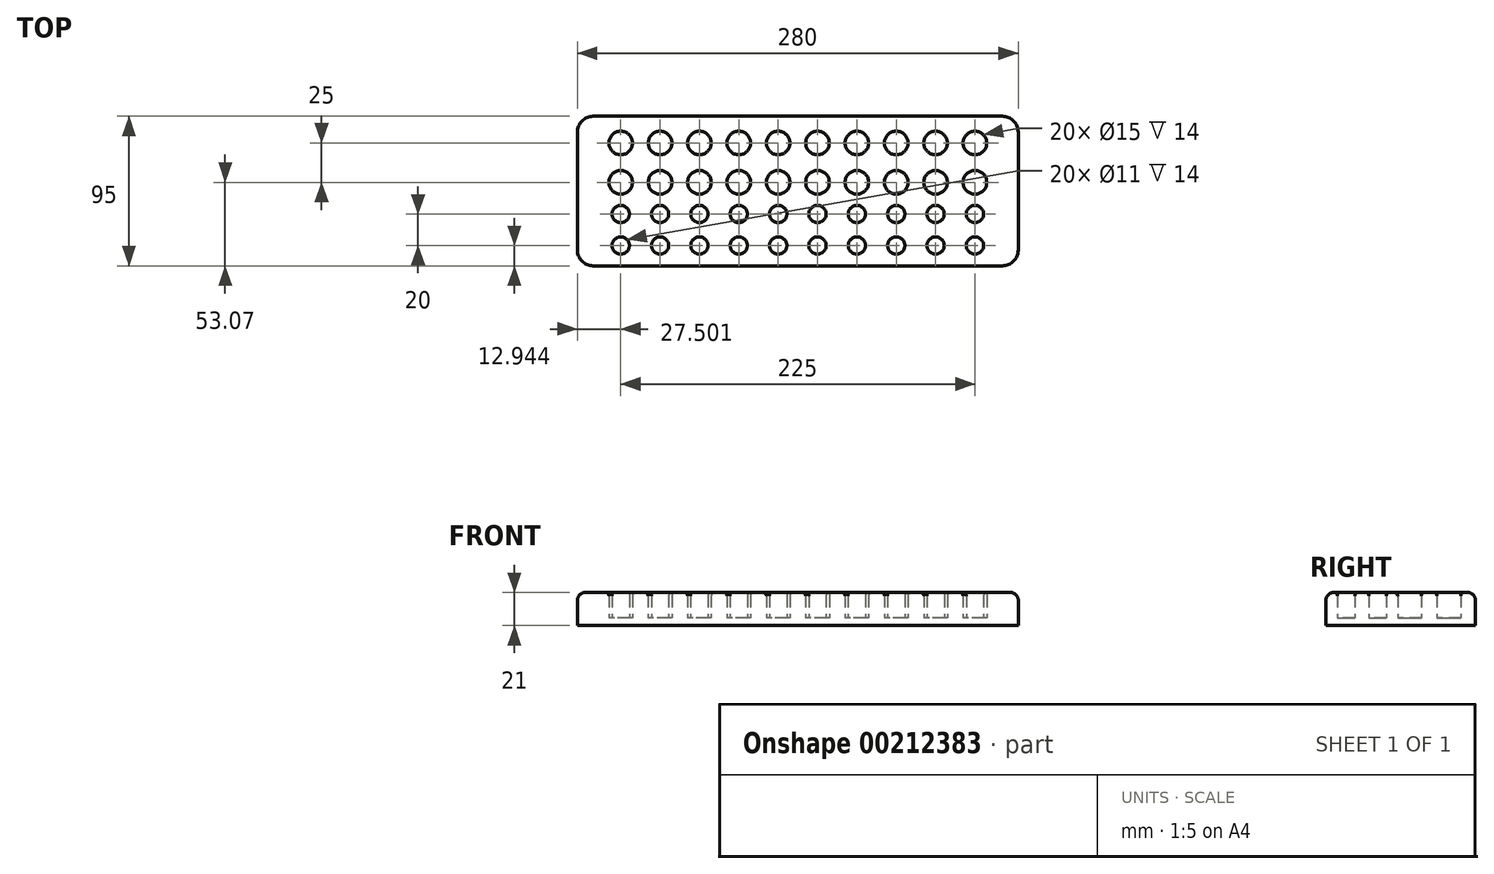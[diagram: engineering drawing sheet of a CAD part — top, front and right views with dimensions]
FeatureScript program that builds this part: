
annotation { "Feature Type Name" : "Feature", "Feature Type Description" : "" }
export const myFeature = defineFeature(function(context is Context, id is Id, definition is map)
    precondition{}
    {
        {
            var Q0;
            Q0=qCreatedBy(makeId("Top.planeOp"),FACE);
            var sketch = newSketch(context, id + "F0", { "sketchPlane" : qUnion([Q0])});
            skLineSegment(sketch, "E0.bottom", {"start": v(-133.18, 16.93) * mm, "end": v(126.82, 16.93) * mm});
            skLineSegment(sketch, "E0.top", {"start": v(-133.18, -78.07) * mm, "end": v(126.82, -78.07) * mm});
            skLineSegment(sketch, "E0.left", {"start": v(-143.18, 6.93) * mm, "end": v(-143.18, -68.07) * mm});
            skLineSegment(sketch, "E0.right", {"start": v(136.82, 6.93) * mm, "end": v(136.82, -68.07) * mm});
            skPoint(sketch, "E1.visualSharp", {"position": v(-143.18, 16.93) * mm});
            skArc(sketch, "E1.filletArc", {"start": v(-133.18, 16.93) * mm, "mid": v(-140.25, 14) * mm, "end": v(-143.18, 6.93) * mm});
            skPoint(sketch, "E2.visualSharp", {"position": v(136.82, 16.93) * mm});
            skArc(sketch, "E2.filletArc", {"start": v(136.82, 6.93) * mm, "mid": v(133.9, 14) * mm, "end": v(126.82, 16.93) * mm});
            skPoint(sketch, "E3.visualSharp", {"position": v(136.82, -78.07) * mm});
            skArc(sketch, "E3.filletArc", {"start": v(126.82, -78.07) * mm, "mid": v(133.9, -75.14) * mm, "end": v(136.82, -68.07) * mm});
            skPoint(sketch, "E4.visualSharp", {"position": v(-143.18, -78.07) * mm});
            skArc(sketch, "E4.filletArc", {"start": v(-143.18, -68.07) * mm, "mid": v(-140.25, -75.14) * mm, "end": v(-133.18, -78.07) * mm});
            skSolve(sketch);
        }
        {
            var Q0;
            Q0 = qSketchRegion(id + "F0", true);
            extrude(context, id + "F1", {"entities" : qUnion([Q0]), "depth" : 21 * mm});
        }
        {
            var Q0;
            Q0=qCreatedBy(makeId("Top.planeOp"),FACE);
            var sketch = newSketch(context, id + "F2", { "sketchPlane" : qUnion([Q0])});
            skCircle(sketch, "E5", {"center": v(-115.68, 0) * mm, "radius": 7.5 * mm});
            skCircle(sketch, "E6.0.1.0", {"center": v(-115.68, -25) * mm, "radius": 7.5 * mm});
            skCircle(sketch, "E6.1.0.0", {"center": v(-90.68, 0) * mm, "radius": 7.5 * mm});
            skCircle(sketch, "E6.1.1.0", {"center": v(-90.68, -25) * mm, "radius": 7.5 * mm});
            skCircle(sketch, "E6.2.0.0", {"center": v(-65.68, 0) * mm, "radius": 7.5 * mm});
            skCircle(sketch, "E6.2.1.0", {"center": v(-65.68, -25) * mm, "radius": 7.5 * mm});
            skCircle(sketch, "E6.3.0.0", {"center": v(-40.68, 0) * mm, "radius": 7.5 * mm});
            skCircle(sketch, "E6.3.1.0", {"center": v(-40.68, -25) * mm, "radius": 7.5 * mm});
            skCircle(sketch, "E6.4.0.0", {"center": v(-15.68, 0) * mm, "radius": 7.5 * mm});
            skCircle(sketch, "E6.4.1.0", {"center": v(-15.68, -25) * mm, "radius": 7.5 * mm});
            skCircle(sketch, "E6.5.0.0", {"center": v(9.32, 0) * mm, "radius": 7.5 * mm});
            skCircle(sketch, "E6.5.1.0", {"center": v(9.32, -25) * mm, "radius": 7.5 * mm});
            skCircle(sketch, "E6.6.0.0", {"center": v(34.32, 0) * mm, "radius": 7.5 * mm});
            skCircle(sketch, "E6.6.1.0", {"center": v(34.32, -25) * mm, "radius": 7.5 * mm});
            skCircle(sketch, "E6.7.0.0", {"center": v(59.32, 0) * mm, "radius": 7.5 * mm});
            skCircle(sketch, "E6.7.1.0", {"center": v(59.32, -25) * mm, "radius": 7.5 * mm});
            skCircle(sketch, "E6.8.0.0", {"center": v(84.32, 0) * mm, "radius": 7.5 * mm});
            skCircle(sketch, "E6.8.1.0", {"center": v(84.32, -25) * mm, "radius": 7.5 * mm});
            skCircle(sketch, "E6.9.0.0", {"center": v(109.32, 0) * mm, "radius": 7.5 * mm});
            skCircle(sketch, "E6.9.1.0", {"center": v(109.32, -25) * mm, "radius": 7.5 * mm});
            skLineSegment(sketch, "E6.direction1", {"start": v(-115.68, 0) * mm, "end": v(-90.68, 0) * mm, "construction": true});
            skLineSegment(sketch, "E6.direction2", {"start": v(-115.68, 0) * mm, "end": v(-115.68, -25) * mm, "construction": true});
            skLineSegment(sketch, "E7", {"start": v(109.32, 0) * mm, "end": v(136.82, 0) * mm, "construction": true});
            skLineSegment(sketch, "E8", {"start": v(-115.68, -12.5) * mm, "end": v(-143.18, -12.5) * mm, "construction": true});
            skCircle(sketch, "E9", {"center": v(-115.68, -45.13) * mm, "radius": 5.5 * mm});
            skLineSegment(sketch, "E10", {"start": v(-115.68, 0) * mm, "end": v(-115.68, -69.49) * mm, "construction": true});
            skCircle(sketch, "E11.0.1.0", {"center": v(-115.68, -65.13) * mm, "radius": 5.5 * mm});
            skCircle(sketch, "E11.1.0.0", {"center": v(-90.68, -45.13) * mm, "radius": 5.5 * mm});
            skCircle(sketch, "E11.1.1.0", {"center": v(-90.68, -65.13) * mm, "radius": 5.5 * mm});
            skCircle(sketch, "E11.2.0.0", {"center": v(-65.68, -45.13) * mm, "radius": 5.5 * mm});
            skCircle(sketch, "E11.2.1.0", {"center": v(-65.68, -65.13) * mm, "radius": 5.5 * mm});
            skCircle(sketch, "E11.3.0.0", {"center": v(-40.68, -45.13) * mm, "radius": 5.5 * mm});
            skCircle(sketch, "E11.3.1.0", {"center": v(-40.68, -65.13) * mm, "radius": 5.5 * mm});
            skCircle(sketch, "E11.4.0.0", {"center": v(-15.68, -45.13) * mm, "radius": 5.5 * mm});
            skCircle(sketch, "E11.4.1.0", {"center": v(-15.68, -65.13) * mm, "radius": 5.5 * mm});
            skCircle(sketch, "E11.5.0.0", {"center": v(9.32, -45.13) * mm, "radius": 5.5 * mm});
            skCircle(sketch, "E11.5.1.0", {"center": v(9.32, -65.13) * mm, "radius": 5.5 * mm});
            skCircle(sketch, "E11.6.0.0", {"center": v(34.32, -45.13) * mm, "radius": 5.5 * mm});
            skCircle(sketch, "E11.6.1.0", {"center": v(34.32, -65.13) * mm, "radius": 5.5 * mm});
            skCircle(sketch, "E11.7.0.0", {"center": v(59.32, -45.13) * mm, "radius": 5.5 * mm});
            skCircle(sketch, "E11.7.1.0", {"center": v(59.32, -65.13) * mm, "radius": 5.5 * mm});
            skCircle(sketch, "E11.8.0.0", {"center": v(84.32, -45.13) * mm, "radius": 5.5 * mm});
            skCircle(sketch, "E11.8.1.0", {"center": v(84.32, -65.13) * mm, "radius": 5.5 * mm});
            skCircle(sketch, "E11.9.0.0", {"center": v(109.32, -45.13) * mm, "radius": 5.5 * mm});
            skCircle(sketch, "E11.9.1.0", {"center": v(109.32, -65.13) * mm, "radius": 5.5 * mm});
            skLineSegment(sketch, "E11.direction1", {"start": v(-115.68, -45.13) * mm, "end": v(-90.68, -45.13) * mm, "construction": true});
            skLineSegment(sketch, "E11.direction2", {"start": v(-115.68, -45.13) * mm, "end": v(-115.68, -65.13) * mm, "construction": true});
            skSolve(sketch);
        }
        {
            var Q0;
            Q0 = qSketchRegion(id + "F2", true);
            var Q1;
            Q1=sQuery(id+"F2.wireOp",EDGE,"E6.3.0.0");
            var Q2;
            Q2=sQuery(id+"F2.wireOp",EDGE,"E6.8.0.0");
            var Q3;
            Q3=sQuery(id+"F2.wireOp",EDGE,"E11.3.1.0");
            var Q4;
            Q4=sQuery(id+"F2.wireOp",EDGE,"E6.2.1.0");
            var Q5;
            Q5=sQuery(id+"F2.wireOp",EDGE,"E6.2.0.0");
            var Q6;
            Q6=sQuery(id+"F2.wireOp",EDGE,"E11.4.0.0");
            var Q7;
            Q7=sQuery(id+"F2.wireOp",EDGE,"E11.2.0.0");
            var Q8;
            Q8=sQuery(id+"F2.wireOp",EDGE,"E6.1.1.0");
            var Q9;
            Q9=sQuery(id+"F2.wireOp",EDGE,"E6.1.0.0");
            var Q10;
            Q10=sQuery(id+"F2.wireOp",EDGE,"E11.5.1.0");
            var Q11;
            Q11=sQuery(id+"F2.wireOp",EDGE,"E6.0.1.0");
            var Q12;
            Q12=sQuery(id+"F2.wireOp",EDGE,"E5");
            var Q13;
            Q13=sQuery(id+"F2.wireOp",EDGE,"E11.7.0.0");
            var Q14;
            Q14=sQuery(id+"F2.wireOp",EDGE,"E6.7.1.0");
            var Q15;
            Q15=sQuery(id+"F2.wireOp",EDGE,"E6.7.0.0");
            var Q16;
            Q16=sQuery(id+"F2.wireOp",EDGE,"E11.1.0.0");
            var Q17;
            Q17=sQuery(id+"F2.wireOp",EDGE,"E11.9.0.0");
            var Q18;
            Q18=sQuery(id+"F2.wireOp",EDGE,"E6.6.1.0");
            var Q19;
            Q19=sQuery(id+"F2.wireOp",EDGE,"E11.9.1.0");
            var Q20;
            Q20=sQuery(id+"F2.wireOp",EDGE,"E11.1.1.0");
            var Q21;
            Q21=sQuery(id+"F2.wireOp",EDGE,"E11.7.1.0");
            var Q22;
            Q22=sQuery(id+"F2.wireOp",EDGE,"E6.8.1.0");
            var Q23;
            Q23=sQuery(id+"F2.wireOp",EDGE,"E9");
            var Q24;
            Q24=sQuery(id+"F2.wireOp",EDGE,"E11.6.0.0");
            var Q25;
            Q25=sQuery(id+"F2.wireOp",EDGE,"E11.2.1.0");
            var Q26;
            Q26=sQuery(id+"F2.wireOp",EDGE,"E6.3.1.0");
            var Q27;
            Q27=sQuery(id+"F2.wireOp",EDGE,"E6.4.0.0");
            var Q28;
            Q28=sQuery(id+"F2.wireOp",EDGE,"E6.4.1.0");
            var Q29;
            Q29=sQuery(id+"F2.wireOp",EDGE,"E6.5.0.0");
            var Q30;
            Q30=sQuery(id+"F2.wireOp",EDGE,"E6.5.1.0");
            var Q31;
            Q31=sQuery(id+"F2.wireOp",EDGE,"E11.8.0.0");
            var Q32;
            Q32=sQuery(id+"F2.wireOp",EDGE,"E6.6.0.0");
            var Q33;
            Q33=sQuery(id+"F2.wireOp",EDGE,"E11.3.0.0");
            var Q34;
            Q34=sQuery(id+"F2.wireOp",EDGE,"E11.6.1.0");
            var Q35;
            Q35=sQuery(id+"F2.wireOp",EDGE,"E11.4.1.0");
            var Q36;
            Q36=sQuery(id+"F2.wireOp",EDGE,"E6.9.0.0");
            var Q37;
            Q37=sQuery(id+"F2.wireOp",EDGE,"E11.8.1.0");
            var Q38;
            Q38=sQuery(id+"F2.wireOp",EDGE,"E11.0.1.0");
            var Q39;
            Q39=sQuery(id+"F2.wireOp",EDGE,"E11.5.0.0");
            var Q40;
            Q40=sQuery(id+"F2.wireOp",EDGE,"E6.9.1.0");
            extrude(context, id + "F3", {"entities" : qUnion([Q0]), "surfaceEntities" : qUnion([Q1, Q2, Q3, Q4, Q5, Q6, Q7, Q8, Q9, Q10, Q11, Q12, Q13, Q14, Q15, Q16, Q17, Q18, Q19, Q20, Q21, Q22, Q23, Q24, Q25, Q26, Q27, Q28, Q29, Q30, Q31, Q32, Q33, Q34, Q35, Q36, Q37, Q38, Q39, Q40]), "depth" : 22 * mm, "hasSecondDirection" : true, "secondDirectionOppositeDirection" : false, "secondDirectionDepth" : 5 * mm});
        }
        {
            var Q0;
            Q0=makeQuery(id+"F1.opExtrude","CAP_FACE",FACE,{"disambiguationData":[OSD([sQuery(id+"F0.wireOp",EDGE,"E0.bottom"),sQuery(id+"F0.wireOp",EDGE,"E0.top"),sQuery(id+"F0.wireOp",EDGE,"E0.left"),sQuery(id+"F0.wireOp",EDGE,"E0.right"),sQuery(id+"F0.wireOp",EDGE,"E1.filletArc"),sQuery(id+"F0.wireOp",EDGE,"E2.filletArc"),sQuery(id+"F0.wireOp",EDGE,"E3.filletArc"),sQuery(id+"F0.wireOp",EDGE,"E4.filletArc")])],"isStart":false});
            fillet(context, id + "F4", {"entities" : qUnion([Q0]), "radius" : 5 * mm, "tangentPropagation" : true, "allowEdgeOverflow" : false});
        }
        {
            var Q0;
            Q0=makeQuery(id+"F3.opExtrude","SWEPT_BODY",BODY,{"disambiguationData":[OSD([sQuery(id+"F2.wireOp",EDGE,"E5")])]});
            var Q1;
            Q1=makeQuery(id+"F3.opExtrude","SWEPT_BODY",BODY,{"disambiguationData":[OSD([sQuery(id+"F2.wireOp",EDGE,"E6.0.1.0")])]});
            var Q2;
            Q2=makeQuery(id+"F3.opExtrude","SWEPT_BODY",BODY,{"disambiguationData":[OSD([sQuery(id+"F2.wireOp",EDGE,"E6.1.0.0")])]});
            var Q3;
            Q3=makeQuery(id+"F3.opExtrude","SWEPT_BODY",BODY,{"disambiguationData":[OSD([sQuery(id+"F2.wireOp",EDGE,"E6.1.1.0")])]});
            var Q4;
            Q4=makeQuery(id+"F3.opExtrude","SWEPT_BODY",BODY,{"disambiguationData":[OSD([sQuery(id+"F2.wireOp",EDGE,"E6.2.0.0")])]});
            var Q5;
            Q5=makeQuery(id+"F3.opExtrude","SWEPT_BODY",BODY,{"disambiguationData":[OSD([sQuery(id+"F2.wireOp",EDGE,"E6.2.1.0")])]});
            var Q6;
            Q6=makeQuery(id+"F3.opExtrude","SWEPT_BODY",BODY,{"disambiguationData":[OSD([sQuery(id+"F2.wireOp",EDGE,"E6.3.0.0")])]});
            var Q7;
            Q7=makeQuery(id+"F3.opExtrude","SWEPT_BODY",BODY,{"disambiguationData":[OSD([sQuery(id+"F2.wireOp",EDGE,"E6.3.1.0")])]});
            var Q8;
            Q8=makeQuery(id+"F3.opExtrude","SWEPT_BODY",BODY,{"disambiguationData":[OSD([sQuery(id+"F2.wireOp",EDGE,"E6.4.0.0")])]});
            var Q9;
            Q9=makeQuery(id+"F3.opExtrude","SWEPT_BODY",BODY,{"disambiguationData":[OSD([sQuery(id+"F2.wireOp",EDGE,"E6.4.1.0")])]});
            var Q10;
            Q10=makeQuery(id+"F3.opExtrude","SWEPT_BODY",BODY,{"disambiguationData":[OSD([sQuery(id+"F2.wireOp",EDGE,"E6.5.0.0")])]});
            var Q11;
            Q11=makeQuery(id+"F3.opExtrude","SWEPT_BODY",BODY,{"disambiguationData":[OSD([sQuery(id+"F2.wireOp",EDGE,"E6.5.1.0")])]});
            var Q12;
            Q12=makeQuery(id+"F3.opExtrude","SWEPT_BODY",BODY,{"disambiguationData":[OSD([sQuery(id+"F2.wireOp",EDGE,"E6.6.0.0")])]});
            var Q13;
            Q13=makeQuery(id+"F3.opExtrude","SWEPT_BODY",BODY,{"disambiguationData":[OSD([sQuery(id+"F2.wireOp",EDGE,"E6.6.1.0")])]});
            var Q14;
            Q14=makeQuery(id+"F3.opExtrude","SWEPT_BODY",BODY,{"disambiguationData":[OSD([sQuery(id+"F2.wireOp",EDGE,"E6.7.0.0")])]});
            var Q15;
            Q15=makeQuery(id+"F3.opExtrude","SWEPT_BODY",BODY,{"disambiguationData":[OSD([sQuery(id+"F2.wireOp",EDGE,"E6.7.1.0")])]});
            var Q16;
            Q16=makeQuery(id+"F3.opExtrude","SWEPT_BODY",BODY,{"disambiguationData":[OSD([sQuery(id+"F2.wireOp",EDGE,"E6.8.0.0")])]});
            var Q17;
            Q17=makeQuery(id+"F3.opExtrude","SWEPT_BODY",BODY,{"disambiguationData":[OSD([sQuery(id+"F2.wireOp",EDGE,"E6.8.1.0")])]});
            var Q18;
            Q18=makeQuery(id+"F3.opExtrude","SWEPT_BODY",BODY,{"disambiguationData":[OSD([sQuery(id+"F2.wireOp",EDGE,"E6.9.0.0")])]});
            var Q19;
            Q19=makeQuery(id+"F3.opExtrude","SWEPT_BODY",BODY,{"disambiguationData":[OSD([sQuery(id+"F2.wireOp",EDGE,"E6.9.1.0")])]});
            var Q20;
            Q20=makeQuery(id+"F3.opExtrude","SWEPT_BODY",BODY,{"disambiguationData":[OSD([sQuery(id+"F2.wireOp",EDGE,"E9")])]});
            var Q21;
            Q21=makeQuery(id+"F3.opExtrude","SWEPT_BODY",BODY,{"disambiguationData":[OSD([sQuery(id+"F2.wireOp",EDGE,"E11.0.1.0")])]});
            var Q22;
            Q22=makeQuery(id+"F3.opExtrude","SWEPT_BODY",BODY,{"disambiguationData":[OSD([sQuery(id+"F2.wireOp",EDGE,"E11.1.0.0")])]});
            var Q23;
            Q23=makeQuery(id+"F3.opExtrude","SWEPT_BODY",BODY,{"disambiguationData":[OSD([sQuery(id+"F2.wireOp",EDGE,"E11.1.1.0")])]});
            var Q24;
            Q24=makeQuery(id+"F3.opExtrude","SWEPT_BODY",BODY,{"disambiguationData":[OSD([sQuery(id+"F2.wireOp",EDGE,"E11.2.0.0")])]});
            var Q25;
            Q25=makeQuery(id+"F3.opExtrude","SWEPT_BODY",BODY,{"disambiguationData":[OSD([sQuery(id+"F2.wireOp",EDGE,"E11.2.1.0")])]});
            var Q26;
            Q26=makeQuery(id+"F3.opExtrude","SWEPT_BODY",BODY,{"disambiguationData":[OSD([sQuery(id+"F2.wireOp",EDGE,"E11.3.0.0")])]});
            var Q27;
            Q27=makeQuery(id+"F3.opExtrude","SWEPT_BODY",BODY,{"disambiguationData":[OSD([sQuery(id+"F2.wireOp",EDGE,"E11.3.1.0")])]});
            var Q28;
            Q28=makeQuery(id+"F3.opExtrude","SWEPT_BODY",BODY,{"disambiguationData":[OSD([sQuery(id+"F2.wireOp",EDGE,"E11.4.0.0")])]});
            var Q29;
            Q29=makeQuery(id+"F3.opExtrude","SWEPT_BODY",BODY,{"disambiguationData":[OSD([sQuery(id+"F2.wireOp",EDGE,"E11.4.1.0")])]});
            var Q30;
            Q30=makeQuery(id+"F3.opExtrude","SWEPT_BODY",BODY,{"disambiguationData":[OSD([sQuery(id+"F2.wireOp",EDGE,"E11.5.0.0")])]});
            var Q31;
            Q31=makeQuery(id+"F3.opExtrude","SWEPT_BODY",BODY,{"disambiguationData":[OSD([sQuery(id+"F2.wireOp",EDGE,"E11.5.1.0")])]});
            var Q32;
            Q32=makeQuery(id+"F3.opExtrude","SWEPT_BODY",BODY,{"disambiguationData":[OSD([sQuery(id+"F2.wireOp",EDGE,"E11.6.0.0")])]});
            var Q33;
            Q33=makeQuery(id+"F3.opExtrude","SWEPT_BODY",BODY,{"disambiguationData":[OSD([sQuery(id+"F2.wireOp",EDGE,"E11.6.1.0")])]});
            var Q34;
            Q34=makeQuery(id+"F3.opExtrude","SWEPT_BODY",BODY,{"disambiguationData":[OSD([sQuery(id+"F2.wireOp",EDGE,"E11.7.0.0")])]});
            var Q35;
            Q35=makeQuery(id+"F3.opExtrude","SWEPT_BODY",BODY,{"disambiguationData":[OSD([sQuery(id+"F2.wireOp",EDGE,"E11.7.1.0")])]});
            var Q36;
            Q36=makeQuery(id+"F3.opExtrude","SWEPT_BODY",BODY,{"disambiguationData":[OSD([sQuery(id+"F2.wireOp",EDGE,"E11.8.0.0")])]});
            var Q37;
            Q37=makeQuery(id+"F3.opExtrude","SWEPT_BODY",BODY,{"disambiguationData":[OSD([sQuery(id+"F2.wireOp",EDGE,"E11.8.1.0")])]});
            var Q38;
            Q38=makeQuery(id+"F3.opExtrude","SWEPT_BODY",BODY,{"disambiguationData":[OSD([sQuery(id+"F2.wireOp",EDGE,"E11.9.0.0")])]});
            var Q39;
            Q39=makeQuery(id+"F3.opExtrude","SWEPT_BODY",BODY,{"disambiguationData":[OSD([sQuery(id+"F2.wireOp",EDGE,"E11.9.1.0")])]});
            var Q40;
            Q40=makeQuery(id+"F1.opExtrude","SWEPT_BODY",BODY,{"disambiguationData":[OSD([sQuery(id+"F0.wireOp",EDGE,"E0.bottom"),sQuery(id+"F0.wireOp",EDGE,"E0.top"),sQuery(id+"F0.wireOp",EDGE,"E0.left"),sQuery(id+"F0.wireOp",EDGE,"E0.right"),sQuery(id+"F0.wireOp",EDGE,"E1.filletArc"),sQuery(id+"F0.wireOp",EDGE,"E2.filletArc"),sQuery(id+"F0.wireOp",EDGE,"E3.filletArc"),sQuery(id+"F0.wireOp",EDGE,"E4.filletArc")])]});
            booleanBodies(context, id + "F5", {"operationType" : BooleanOperationType.SUBTRACTION, "tools" : qUnion([Q0, Q1, Q2, Q3, Q4, Q5, Q6, Q7, Q8, Q9, Q10, Q11, Q12, Q13, Q14, Q15, Q16, Q17, Q18, Q19, Q20, Q21, Q22, Q23, Q24, Q25, Q26, Q27, Q28, Q29, Q30, Q31, Q32, Q33, Q34, Q35, Q36, Q37, Q38, Q39]), "targets" : qUnion([Q40])});
        }
        {
            var Q0;
            Q0=makeQuery(id+"F1.opExtrude","CAP_FACE",FACE,{"disambiguationData":[OSD([sQuery(id+"F0.wireOp",EDGE,"E0.bottom"),sQuery(id+"F0.wireOp",EDGE,"E0.top"),sQuery(id+"F0.wireOp",EDGE,"E0.left"),sQuery(id+"F0.wireOp",EDGE,"E0.right"),sQuery(id+"F0.wireOp",EDGE,"E1.filletArc"),sQuery(id+"F0.wireOp",EDGE,"E2.filletArc"),sQuery(id+"F0.wireOp",EDGE,"E3.filletArc"),sQuery(id+"F0.wireOp",EDGE,"E4.filletArc")])],"isStart":false});
            fillet(context, id + "F6", {"entities" : qUnion([Q0]), "radius" : 2 * mm, "tangentPropagation" : true, "allowEdgeOverflow" : false});
        }
    });
